# Revit family: QF_Vollrath_59502DW
name_source: partatom
category: Specialty Equipment
revit_build: Autodesk Revit 2016 (Build: 20151007_0715(x64)
units: mm (PartAtom-declared; Revit-internal decimal feet)

## family parameters
Always vertical = Yes
Cut with Voids When Loaded = No
OmniClass Number = 23.40.40.00
OmniClass Title = Food Service Equipment and Furnishings
Part Type = Normal
Room Calculation Point = No
Round Connector Dimension = Use Diameter
Shared = No
Work Plane-Based = Yes

## types (1)
- QF_Vollrath_59502DW
    Apparent Power = 312 VA
    Conn Plug = NEMA 5-15P
    Cycle = 60 Hz
    Default Elevation = 0.00"
    Depth = 16.06"
    Description = Countertop Induction Range
    Elec Conn Connection Height = 2.00"
    FL Amps = 3 A
    Foodservice Equipment Identifier = Yes
    Manufacturer = Vollrath
    Model = 59502DW
    Phase = 1
    Volts = 120 V
    Watts = 300 W
    Weight in Pounds = 0
    Width = 16.06"

## geometry (parser evidence)
native form markers: Blend x4, Sweep x3
no freeform markers — native parametric forms only
